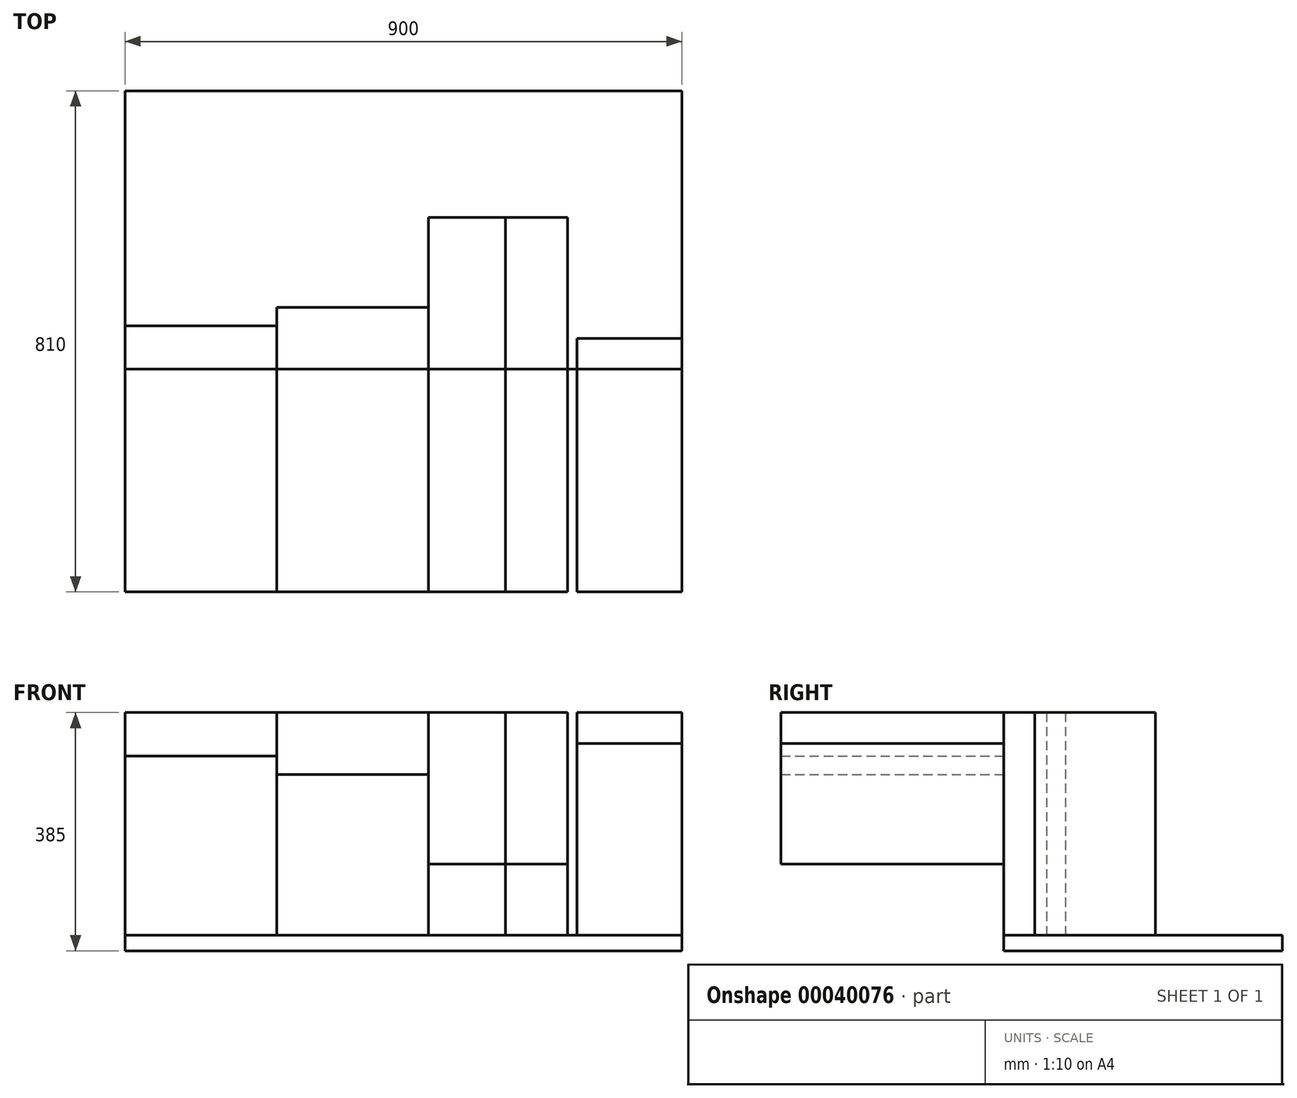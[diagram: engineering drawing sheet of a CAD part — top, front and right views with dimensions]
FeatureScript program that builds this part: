
annotation { "Feature Type Name" : "Feature", "Feature Type Description" : "" }
export const myFeature = defineFeature(function(context is Context, id is Id, definition is map)
    precondition{}
    {
        {
            var Q0;
            Q0=qCreatedBy(makeId("Front.planeOp"),FACE);
            var sketch = newSketch(context, id + "F0", { "sketchPlane" : qUnion([Q0])});
            skLineSegment(sketch, "E0.bottom", {"start": v(450, -12.5) * mm, "end": v(-450, -12.5) * mm});
            skLineSegment(sketch, "E0.top", {"start": v(450, 12.5) * mm, "end": v(-450, 12.5) * mm});
            skLineSegment(sketch, "E0.left", {"start": v(450, -12.5) * mm, "end": v(450, 12.5) * mm});
            skLineSegment(sketch, "E0.right", {"start": v(-450, -12.5) * mm, "end": v(-450, 12.5) * mm});
            skPoint(sketch, "E0.middle", {"position": v(0, 0) * mm});
            skLineSegment(sketch, "E1.bottom", {"start": v(-450, 12.5) * mm, "end": v(-205, 12.5) * mm});
            skLineSegment(sketch, "E1.top", {"start": v(-450, 372.5) * mm, "end": v(-205, 372.5) * mm});
            skLineSegment(sketch, "E1.left", {"start": v(-450, 12.5) * mm, "end": v(-450, 372.5) * mm});
            skLineSegment(sketch, "E1.right", {"start": v(-205, 12.5) * mm, "end": v(-205, 372.5) * mm});
            skLineSegment(sketch, "E2.bottom", {"start": v(450, 12.5) * mm, "end": v(280, 12.5) * mm});
            skLineSegment(sketch, "E2.top", {"start": v(450, 372.5) * mm, "end": v(280, 372.5) * mm});
            skLineSegment(sketch, "E2.left", {"start": v(450, 12.5) * mm, "end": v(450, 372.5) * mm});
            skLineSegment(sketch, "E2.right", {"start": v(280, 12.5) * mm, "end": v(280, 372.5) * mm});
            skLineSegment(sketch, "E3.bottom", {"start": v(-205, 12.5) * mm, "end": v(40, 12.5) * mm});
            skLineSegment(sketch, "E3.top", {"start": v(-205, 372.5) * mm, "end": v(40, 372.5) * mm});
            skLineSegment(sketch, "E3.right", {"start": v(40, 12.5) * mm, "end": v(40, 372.5) * mm});
            skLineSegment(sketch, "E4.bottom", {"start": v(40, 12.5) * mm, "end": v(165, 12.5) * mm});
            skLineSegment(sketch, "E4.top", {"start": v(40, 372.5) * mm, "end": v(165, 372.5) * mm});
            skLineSegment(sketch, "E5.left", {"start": v(165, 12.5) * mm, "end": v(165, 372.5) * mm});
            skLineSegment(sketch, "E6.bottom", {"start": v(165, 12.5) * mm, "end": v(265, 12.5) * mm});
            skLineSegment(sketch, "E6.top", {"start": v(165, 372.5) * mm, "end": v(265, 372.5) * mm});
            skLineSegment(sketch, "E6.right", {"start": v(265, 12.5) * mm, "end": v(265, 372.5) * mm});
            skSolve(sketch);
        }
        {
            var Q0;
            Q0=makeQuery(id+"F0.imprint","IMPRINT",FACE,{"disambiguationData":[TD([[makeQuery(id+"F0.imprint","IMPRINT",EDGE,{"derivedFrom":sQuery(id+"F0.wireOp",EDGE,"E0.bottom")}),-1.0]])]});
            extrude(context, id + "F1", {"entities" : qUnion([Q0]), "oppositeDirection" : true, "depth" : 450 * mm});
        }
        {
            var Q0;
            Q0=makeQuery(id+"F0.imprint","IMPRINT",FACE,{"disambiguationData":[TD([[makeQuery(id+"F0.imprint","IMPRINT",EDGE,{"derivedFrom":sQuery(id+"F0.wireOp",EDGE,"E1.top")}),-1.0]])]});
            extrude(context, id + "F2", {"entities" : qUnion([Q0]), "oppositeDirection" : true, "depth" : 70 * mm});
        }
        {
            var Q0;
            Q0=makeQuery(id+"F0.imprint","IMPRINT",FACE,{"disambiguationData":[TD([[makeQuery(id+"F0.imprint","IMPRINT",EDGE,{"derivedFrom":sQuery(id+"F0.wireOp",EDGE,"E2.top")}),1.0]])]});
            extrude(context, id + "F3", {"entities" : qUnion([Q0]), "oppositeDirection" : true, "depth" : 50 * mm});
        }
        {
            var Q0;
            {var subQ0=sQuery(id+"F0.wireOp",EDGE,"E1.right");Q0=makeQuery(id+"F0.imprint","IMPRINT",FACE,{"disambiguationData":[TD([[makeQuery(id+"F0.imprint","IMPRINT",EDGE,{"derivedFrom":subQ0}),-1.0]])]});}
            extrude(context, id + "F4", {"entities" : qUnion([Q0]), "oppositeDirection" : true, "depth" : 100 * mm});
        }
        {
            var Q0;
            {var subQ0=sQuery(id+"F0.wireOp",EDGE,"E3.right");Q0=makeQuery(id+"F0.imprint","IMPRINT",FACE,{"disambiguationData":[TD([[makeQuery(id+"F0.imprint","IMPRINT",EDGE,{"derivedFrom":subQ0}),-1.0]])]});}
            extrude(context, id + "F5", {"entities" : qUnion([Q0]), "oppositeDirection" : true, "depth" : 245 * mm});
        }
        {
            var Q0;
            {var subQ2=sQuery(id+"F0.wireOp",EDGE,"E5.left");Q0=makeQuery(id+"F0.imprint","IMPRINT",FACE,{"disambiguationData":[TD([[makeQuery(id+"F0.imprint","IMPRINT",EDGE,{"derivedFrom":subQ2}),-1.0]])]});}
            extrude(context, id + "F6", {"entities" : qUnion([Q0]), "oppositeDirection" : true, "depth" : 245 * mm});
        }
        {
            var Q0;
            Q0=makeQuery(id+"F2.opExtrude","SWEPT_BODY",BODY,{"disambiguationData":[OSD([sQuery(id+"F0.wireOp",EDGE,"E0.top"),sQuery(id+"F0.wireOp",EDGE,"E1.top"),sQuery(id+"F0.wireOp",EDGE,"E1.left"),sQuery(id+"F0.wireOp",EDGE,"E1.right")])]});
            var Q1;
            Q1=makeQuery(id+"F4.opExtrude","SWEPT_BODY",BODY,{"disambiguationData":[OSD([sQuery(id+"F0.wireOp",EDGE,"E0.top"),sQuery(id+"F0.wireOp",EDGE,"E1.right"),sQuery(id+"F0.wireOp",EDGE,"E3.top"),sQuery(id+"F0.wireOp",EDGE,"E3.right")])]});
            var Q2;
            Q2=makeQuery(id+"F5.opExtrude","SWEPT_BODY",BODY,{"disambiguationData":[OSD([sQuery(id+"F0.wireOp",EDGE,"E0.top"),sQuery(id+"F0.wireOp",EDGE,"E3.right"),sQuery(id+"F0.wireOp",EDGE,"E4.top"),sQuery(id+"F0.wireOp",EDGE,"E5.left")])]});
            var Q3;
            Q3=makeQuery(id+"F6.opExtrude","SWEPT_BODY",BODY,{"disambiguationData":[OSD([sQuery(id+"F0.wireOp",EDGE,"E0.top"),sQuery(id+"F0.wireOp",EDGE,"E5.left"),sQuery(id+"F0.wireOp",EDGE,"E6.top"),sQuery(id+"F0.wireOp",EDGE,"E6.right")])]});
            var Q4;
            Q4=makeQuery(id+"F3.opExtrude","SWEPT_BODY",BODY,{"disambiguationData":[OSD([sQuery(id+"F0.wireOp",EDGE,"E0.top"),sQuery(id+"F0.wireOp",EDGE,"E2.top"),sQuery(id+"F0.wireOp",EDGE,"E2.left"),sQuery(id+"F0.wireOp",EDGE,"E2.right")])]});
            var Q5;
            Q5=makeQuery(id+"F3.opExtrude","CAP_EDGE",EDGE,{"disambiguationData":[OSD([sQuery(id+"F0.wireOp",EDGE,"E2.top")])],"isStart":true});
            transform(context, id + "F7", {"entities" : qUnion([Q0, Q1, Q2, Q3, Q4]), "transformType" : TransformType.ROTATION, "transformAxis" : qUnion([Q5]), "angle" : 90 * degree, "makeCopy" : true});
        }
    });
